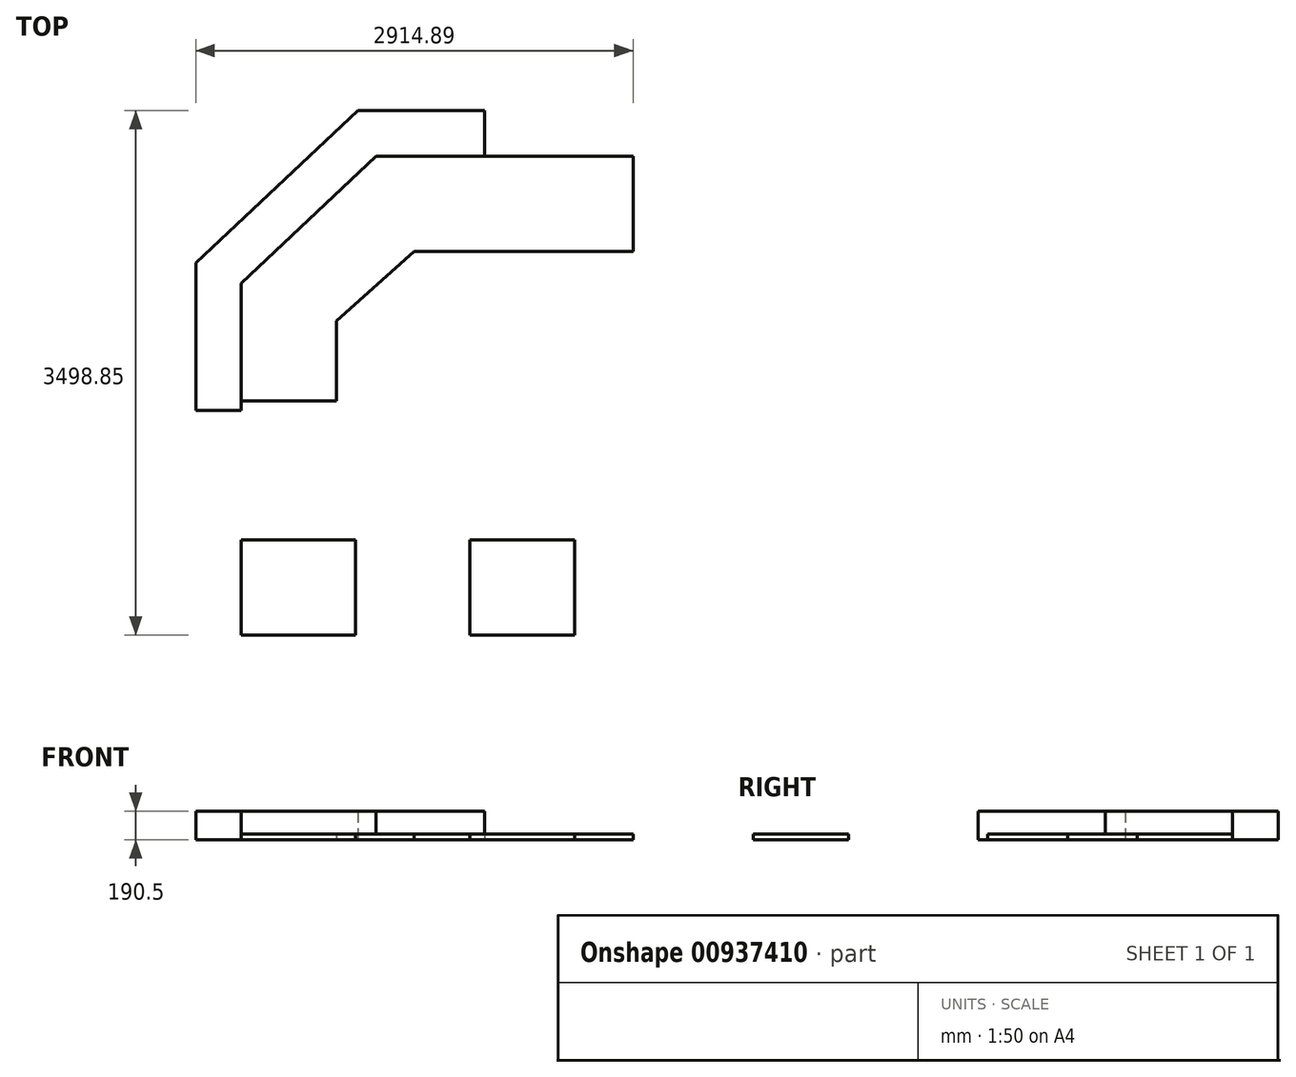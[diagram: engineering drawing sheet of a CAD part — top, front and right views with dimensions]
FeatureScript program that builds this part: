
annotation { "Feature Type Name" : "Feature", "Feature Type Description" : "" }
export const myFeature = defineFeature(function(context is Context, id is Id, definition is map)
    precondition{}
    {
        {
            var Q0;
            Q0=qCreatedBy(makeId("Top.planeOp"),FACE);
            var sketch = newSketch(context, id + "F0", { "sketchPlane" : qUnion([Q0])});
            skLineSegment(sketch, "E0", {"start": v(0, 0) * mm, "end": v(-1460.5, 0) * mm});
            skLineSegment(sketch, "E1", {"start": v(-1460.5, 0) * mm, "end": v(-1978.76, -463.55) * mm});
            skLineSegment(sketch, "E2", {"start": v(-1978.76, -463.55) * mm, "end": v(-1978.76, -996.95) * mm});
            skLineSegment(sketch, "E3", {"start": v(-1978.76, -996.95) * mm, "end": v(-2613.76, -996.95) * mm});
            skLineSegment(sketch, "E4", {"start": v(-2613.76, -996.95) * mm, "end": v(-2613.76, -212.73) * mm});
            skLineSegment(sketch, "E5", {"start": v(-2613.76, -212.73) * mm, "end": v(-1712.14, 635) * mm});
            skLineSegment(sketch, "E6", {"start": v(-1712.14, 635) * mm, "end": v(0, 635) * mm});
            skLineSegment(sketch, "E7", {"start": v(0, 635) * mm, "end": v(0, 0) * mm});
            skLineSegment(sketch, "E8", {"start": v(-990.6, 635) * mm, "end": v(-990.6, 939.8) * mm});
            skLineSegment(sketch, "E9", {"start": v(-1832.93, 939.8) * mm, "end": v(-2914.9, -77.49) * mm});
            skLineSegment(sketch, "E10", {"start": v(-990.6, 939.8) * mm, "end": v(-1832.93, 939.8) * mm});
            skLineSegment(sketch, "E11", {"start": v(-2613.76, -1060.45) * mm, "end": v(-2918.56, -1060.45) * mm});
            skLineSegment(sketch, "E12", {"start": v(-2914.9, -77.49) * mm, "end": v(-2914.9, -1060.45) * mm});
            skLineSegment(sketch, "E13", {"start": v(-2613.76, -996.95) * mm, "end": v(-2613.76, -1060.45) * mm});
            skSolve(sketch);
        }
        {
            var Q0;
            Q0=makeQuery(id+"F0.imprint","IMPRINT",FACE,{"disambiguationData":[TD([[makeQuery(id+"F0.imprint","IMPRINT",EDGE,{"derivedFrom":sQuery(id+"F0.wireOp",EDGE,"E0")}),-1.0]])]});
            var Q1;
            Q1 = qSketchRegion(id + "FDwDdkh4gkyqwDv_1", true);
            extrude(context, id + "F1", {"entities" : qUnion([Q0, Q1]), "depth" : 38.1 * mm, "offsetDistance" : 25.4 * mm});
        }
        {
            var Q0;
            Q0=makeQuery(id+"F0.imprint","IMPRINT",FACE,{"disambiguationData":[TD([[makeQuery(id+"F0.imprint","IMPRINT",EDGE,{"derivedFrom":sQuery(id+"F0.wireOp",EDGE,"E4")}),1.0]])]});
            extrude(context, id + "F2", {"entities" : qUnion([Q0]), "operationType" : NewBodyOperationType.ADD, "depth" : 190.5 * mm, "offsetDistance" : 25.4 * mm});
        }
        {
            var Q0;
            Q0=qCreatedBy(makeId("Top.planeOp"),FACE);
            var sketch = newSketch(context, id + "F3", { "sketchPlane" : qUnion([Q0])});
            skLineSegment(sketch, "E14.bottom", {"start": v(-2613.76, -1924.05) * mm, "end": v(-1851.76, -1924.05) * mm});
            skLineSegment(sketch, "E14.top", {"start": v(-2613.76, -2559.05) * mm, "end": v(-1851.76, -2559.05) * mm});
            skLineSegment(sketch, "E14.left", {"start": v(-2613.76, -1924.05) * mm, "end": v(-2613.76, -2559.05) * mm});
            skLineSegment(sketch, "E14.right", {"start": v(-1851.76, -1924.05) * mm, "end": v(-1851.76, -2559.05) * mm});
            skLineSegment(sketch, "E15.bottom", {"start": v(-1089.76, -1924.05) * mm, "end": v(-391.26, -1924.05) * mm});
            skLineSegment(sketch, "E15.top", {"start": v(-1089.76, -2559.05) * mm, "end": v(-391.26, -2559.05) * mm});
            skLineSegment(sketch, "E15.left", {"start": v(-1089.76, -1924.05) * mm, "end": v(-1089.76, -2559.05) * mm});
            skLineSegment(sketch, "E15.right", {"start": v(-391.26, -1924.05) * mm, "end": v(-391.26, -2559.05) * mm});
            skSolve(sketch);
        }
        {
            var Q0;
            Q0=makeQuery(id+"F3.imprint","IMPRINT",FACE,{"disambiguationData":[TD([[makeQuery(id+"F3.imprint","IMPRINT",EDGE,{"derivedFrom":sQuery(id+"F3.wireOp",EDGE,"E14.bottom")}),-1.0]])]});
            var Q1;
            Q1=makeQuery(id+"F3.imprint","IMPRINT",FACE,{"disambiguationData":[TD([[makeQuery(id+"F3.imprint","IMPRINT",EDGE,{"derivedFrom":sQuery(id+"F3.wireOp",EDGE,"E15.bottom")}),-1.0]])]});
            extrude(context, id + "F4", {"entities" : qUnion([Q0, Q1]), "depth" : 38.1 * mm, "offsetDistance" : 25.4 * mm});
        }
    });
